# Revit family: FalsoTecho_THU_Lama-Italia-30
name_source: partatom
category: Modelos genéricos
revit_build: Autodesk Revit 2016 (Build: 20160720_0715(x64)
units: mm (PartAtom-declared; Revit-internal decimal feet)

## family parameters
Compartido = No
Corte con vacíos al cargar = Sí
Cota de conector redondo = Diámetro de uso
Número OmniClass = 23.35.70.24.11.17.14.11
Puede alojar armadura = No
Punto de cálculo de habitación = No
Se basa en plano de trabajo = Sí
Siempre vertical = No
Tipo de pieza = Normal
Título OmniClass = Metal Linear Ceilings

## types (2) — shared parameters
COBie Type Category = L387 : Suspended ceilings
Comentarios de tipo = Lamas Italia 30 para techo suspendido, para ser montadas en interior de edificios con rastreles Italia.
Declaración de prestaciones = http://thu.es
Descripción = Falso techo metálico formado por lamas de aluminio prelacadas, encajadas en rastreles de dediferentes pasos de troquelado de (50,60,70,80,90,100mm) y colgadas del forjado superior mediante un sistema de varillas roscadas. Las lamas tienen un ancho de 30 mm y al colocarse en el rastrel quedan separadas una distancia entre sí que dependerá del rastrel seleccionado (20/30/40/50/60/70mm). Opción de Lamas Perforadas: Las lamas pueden presentar un microperforado de 1,5 mm de diámetro al tresbolillo, que abarca la parte central de la lama y 20 mm de cada lateral. El porcentaje de perforación de la lama es del 15,5% teniendo en cuenta los laterales perforados. Las lamas perforadas se suministran con un velo acústico de 0,2 mm de espesor, fijado a la cara interior mediante un adhesivo de activación térmica y un film de protección en su cara vista exterior.
Fabricante = THU Perfil S.L.
Falso techo_Grosor = 75 mm
Famila del producto = Techos metálicos
Ficha resumen = http://thu.es
Ficha técnica = http://thu.es
Grupo del producto = Lamas
IFC Classification = Ceiling
Lama_Altura = 37 mm  [stored 0.121391 ft]
Lama_Anchura = 30 mm  [stored 0.0984252 ft]
Manual de montaje = http://thu.es
Marca = THU
NBS Reference = 20-10-10/110
NBS Reference Description = Board suspended ceiling system
Nombre del objeto = Lama Italia 30
Omniclass = 23.35.70.24.11.17.14.11
País de diseño = España
País de fabricación = España
Página web del fabricante = http://thu.es
Página web del producto = http://thu.es
Rastrel_Altura = 38 mm  [stored 0.124672 ft]
Rastrel_Anchura = 35 mm  [stored 0.114829 ft]
Solape vertical_Lama y rastrel = 6 mm  [stored 0.019685 ft]
THU_Lama_Material = Aluminio
THU_Rastrel = Rastrel_THU_Italia-30 : 3.00x0.56x0.31
THU_Reacción al fuego = A2-s1, d0
THU_Subestructura_Material = Acero galvanizado
zero-valued in all types: Elevación por defecto

## per-type parameters (varying)
| type | Número de edición (versión) | THU_Acabado | THU_Lama | THU_Velo |
| Aluminio_Liso_30x37mm | 0 | Acabado_THU_Lama-Italia-30 : Liso | Lama_THU_Italia-30 : Aluminio_Liso_30x37mm | No |
| Aluminio_Perforado-c/Velo_30x37mm | 1 | Acabado_THU_Lama-Italia-30 : Perforado_Ø1.5mm | Lama_THU_Italia-30 : Aluminio_Perforado-c/Velo_30x37mm | Sí |

note: [stored X ft] marks values corroborated as IEEE doubles in the binary element streams (Revit-internal decimal feet)
